# Revit family: LSC-3G
name_source: partatom
category: Lighting Fixtures
revit_build: Autodesk Revit 2018 (Build: 20181015_0930(x64)
units: mm (PartAtom-declared; Revit-internal decimal feet)

## family parameters
Always vertical = Yes
Cut with Voids When Loaded = No
Light Source = Yes
OmniClass Number = 23.80.70.00
OmniClass Title = Lighting
Part Type = Normal
Room Calculation Point = No
Round Connector Dimension = Use Diameter
Shared = No
Work Plane-Based = No

## types (3) — shared parameters
Color Filter = 16777215
Dimming Lamp Color Temperature Shift = <None>
LSC die casting housing = LSC die casting housing
Spot Beam Angle = 30.00°
Spot Field Angle = 90.00°
Tilt Angle = 90.00°
knock hole = knock hole
lsc shade = lsc shade
mount height = 1200 mm
mounting bracket = mounting bracket
voltage = 277 V

## per-type parameters (varying)
| type | Apparent Load | Light Source Symbol Length |
| LSC-3G 27LED | 27 VA | 300 mm |
| LSC-3G 40LED | 40 VA | 3048 mm  [stored 10 ft] |
| LSC-3G 60LED | 60 VA | 3048 mm  [stored 10 ft] |

note: [stored X ft] marks values corroborated as IEEE doubles in the binary element streams (Revit-internal decimal feet)

## geometry (parser evidence)
native form markers: Sweep x5
no freeform markers — native parametric forms only
